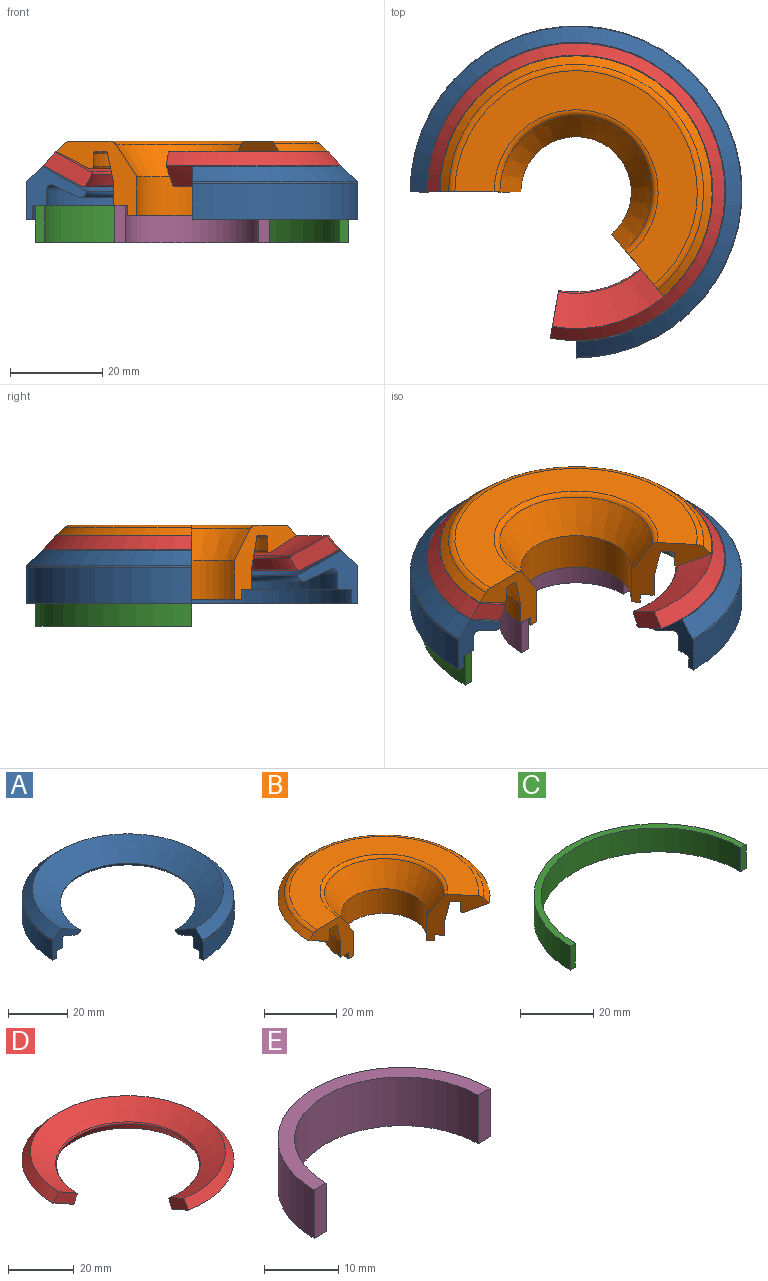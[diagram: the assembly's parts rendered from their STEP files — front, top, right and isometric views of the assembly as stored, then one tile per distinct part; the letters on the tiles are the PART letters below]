
ASSEMBLY  parts=5 mates=4
PART A: 13 faces, bbox 77.8x77.8x11.5 mm
  f0: torus R=35.46mm, axis (0,0,1), area 66.4mm2, adj f1,f10,f11,f12
  f1: cylinder r=35.96mm len=71.92mm, axis (0,0,1), area 1320.5mm2, adj f0,f2,f11,f12
  f2: plane 71.92x71.92mm, normal (0,0,-1), area 248.9mm2, adj f1,f3,f11,f12
  f3: cylinder r=34.46mm len=68.92mm, axis (0,0,1), area 487.1mm2, adj f2,f4,f11,f12
  f4: plane 68.92x68.92mm, normal (0,0,-1), area 465.9mm2, adj f3,f5,f11,f12
  f5: cylinder r=31.46mm len=62.92mm, axis (0,0,1), area 518.8mm2, adj f4,f6,f11,f12
  f6: torus R=30.46mm, axis (0,0,1), area 294.1mm2, adj f5,f7,f11,f12
  f7: cone r=30.02mm half-angle=64.3deg, axis (0,0,1), area 750.7mm2, adj f6,f8,f11,f12
  f8: torus R=24.21mm, axis (0,0,1), area 293.2mm2, adj f7,f9,f11,f12
  f9: cone r=32.42mm half-angle=60deg, axis (0,0,1), area 1433.7mm2, adj f8,f10,f11,f12
  f10: cone r=35.81mm half-angle=45deg, axis (0,0,-1), area 770.6mm2, adj f0,f9,f11,f12
  f11: plane 13.06x11.54mm, normal (-1,0,0), area 57.2mm2, adj f0,f1,f2,f3,f4,f5,f6,f7
  f12: plane 13.06x11.54mm, normal (0,-1,0), area 57.2mm2, adj f0,f1,f2,f3,f4,f5,f6,f7
PART B: 19 faces, bbox 59.9x52.9x16.1 mm
  f0: cone r=16.96mm half-angle=12.3deg, axis (0,0,1), area 461mm2, adj f1,f16,f17,f18
  f1: cylinder r=16.96mm len=33.92mm, axis (0,0,1), area 340.4mm2, adj f0,f2,f17,f18
  f2: plane 33.92x29.95mm, normal (0,0,-1), area 186.2mm2, adj f1,f3,f17,f18
  f3: cylinder r=13.96mm len=27.92mm, axis (0,0,1), area 116.2mm2, adj f2,f4,f17,f18
  f4: plane 27.92x24.65mm, normal (0,0,-1), area 104mm2, adj f3,f5,f17,f18
  f5: cylinder r=11.96mm len=23.92mm, axis (0,0,1), area 401.5mm2, adj f4,f6,f17,f18
  f6: cone r=11.96mm half-angle=33deg, axis (0,0,1), area 478.6mm2, adj f5,f7,f17,f18
  f7: torus R=17.77mm, axis (0,0,1), area 102.4mm2, adj f6,f8,f17,f18
  f8: plane 52.5x46.36mm, normal (0,0,1), area 749mm2, adj f7,f9,f17,f18
  f9: torus R=26.25mm, axis (0,0,1), area 162mm2, adj f8,f10,f17,f18
  f10: cone r=29.46mm half-angle=47.1deg, axis (0,0,-1), area 288.8mm2, adj f9,f11,f17,f18
  f11: cone r=29.46mm half-angle=63.3deg, axis (0,0,1), area 851.1mm2, adj f10,f12,f17,f18
  f12: torus R=21.89mm, axis (0,0,1), area 87.7mm2, adj f11,f13,f17,f18
  f13: cone r=21.39mm half-angle=1.2deg, axis (0,0,-1), area 237.6mm2, adj f12,f14,f17,f18
  f14: torus R=20.83mm, axis (0,0,1), area 65.8mm2, adj f13,f15,f17,f18
  f15: plane 41.67x36.79mm, normal (0,0,-1), area 159.2mm2, adj f14,f16,f17,f18
  f16: torus R=18.83mm, axis (0,0,1), area 50.5mm2, adj f0,f15,f17,f18
  f17: plane 16.07x13.41mm, normal (-0.77,-0.64,0), area 101.5mm2, adj f0,f1,f2,f3,f4,f5,f6,f7
  f18: plane 17.5x16.07mm, normal (0,-1,0), area 101.5mm2, adj f0,f1,f2,f3,f4,f5,f6,f7
PART C: 6 faces, bbox 67.9x34x8 mm
  f0: plane 67.92x33.96mm, normal (0,0,-1), area 207.1mm2, adj f1,f3,f4,f5
  f1: cylinder r=31.96mm len=63.92mm, axis (0,0,1), area 803.2mm2, adj f0,f2,f4,f5
  f2: plane 67.92x33.96mm, normal (0,0,1), area 207.1mm2, adj f1,f3,f4,f5
  f3: cylinder r=33.96mm len=67.92mm, axis (0,0,1), area 853.5mm2, adj f0,f2,f4,f5
  f4: plane 8x2mm, normal (0,-1,0), area 16mm2, adj f0,f1,f2,f3
  f5: plane 8x2mm, normal (0,-1,0), area 16mm2, adj f0,f1,f2,f3
PART D: 8 faces, bbox 64.4x64.4x7.6 mm
  f0: cone r=29.61mm half-angle=40.9deg, axis (0,0,-1), area 599.6mm2, adj f1,f5,f6,f7
  f1: cone r=32.21mm half-angle=61.9deg, axis (0,0,1), area 1317.9mm2, adj f0,f2,f6,f7
  f2: torus R=23.46mm, axis (0,0,1), area 89.5mm2, adj f1,f3,f6,f7
  f3: cone r=23.02mm half-angle=28.1deg, axis (0,0,-1), area 290.9mm2, adj f2,f4,f6,f7
  f4: torus R=22.21mm, axis (0,0,1), area 82.3mm2, adj f3,f5,f6,f7
  f5: cone r=21.96mm half-angle=60.6deg, axis (0,0,1), area 1106.2mm2, adj f0,f4,f6,f7
  f6: plane 10.34x7.6mm, normal (-0.98,0.17,0), area 36.4mm2, adj f0,f1,f2,f3,f4,f5
  f7: plane 10.5x7.6mm, normal (0,-1,0), area 36.4mm2, adj f0,f1,f2,f3,f4,f5
PART E: 6 faces, bbox 33.4x16.7x8 mm
  f0: plane 33.42x16.71mm, normal (0,0,-1), area 110.1mm2, adj f1,f3,f4,f5
  f1: cylinder r=14.46mm len=28.92mm, axis (0,0,1), area 363.4mm2, adj f0,f2,f4,f5
  f2: plane 33.42x16.71mm, normal (0,0,1), area 110.1mm2, adj f1,f3,f4,f5
  f3: cylinder r=16.71mm len=33.42mm, axis (0,0,1), area 419.9mm2, adj f0,f2,f4,f5
  f4: plane 8x2.25mm, normal (0,-1,0), area 18mm2, adj f0,f1,f2,f3
  f5: plane 8x2.25mm, normal (0,-1,0), area 18mm2, adj f0,f1,f2,f3
PLACE A t=(5.38,-2.19,0.07)mm
PLACE B t=(5.38,-2.19,0)mm
PLACE C t=(5.38,-2.19,-7.93)mm
PLACE D t=(5.38,-2.19,-0.07)mm
PLACE E t=(5.38,-2.19,-8)mm
MATE revolute A.f8 <-> C.f1  axis (0,0,-1) through (5.34,-2.19,0.07)mm
MATE cylindrical D.f3 <-> E.f1  axis (0,0,1) through (5.34,-2.19,7.36)mm
MATE revolute B.f0 <-> E.f1  axis (0,0,-1) through (5.34,-2.19,0)mm
MATE slider C.f1 <-> E.f1  axis (0,0,-1) through (5.34,-2.19,-7.93)mm
